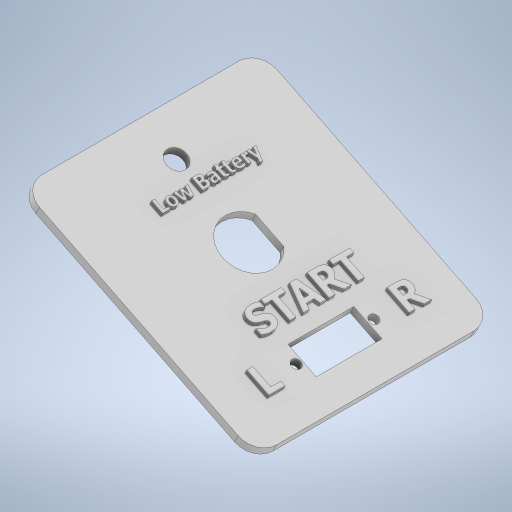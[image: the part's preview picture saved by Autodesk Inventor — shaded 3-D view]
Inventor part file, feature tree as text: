
AUTODESK INVENTOR PART (.ipt)
format: ipt  version: 2024.2 (Build 282272000, 272)  size: 855,552 bytes
history: native  units: mm
features: sketch x10, extrude x9, projected_geometry x4, fillet x2, emboss x1
ambient origin geometry x8: Origin, YZ Plane, XZ Plane, XY Plane, X Axis, Y Axis, Z Axis, Center Point
bodies: Solid1 (feature_tree)
feature tree (26):
  extrude  "Extrusion1"  Depth=2.0mm
  extrude  "Extrusion2"  Depth=6.5mm
  extrude  "Extrusion3"  Depth=9.0mm TaperAngle=0.0deg
  extrude  "Extrusion5"  Depth=9.0mm TaperAngle=0.0deg
  emboss  "Emboss1"
  extrude  "Extrusion6"  Depth=20.0mm
  extrude  "Extrusion7"  Depth=5.0mm
  extrude  "Extrusion8"  Depth=16.3mm
  extrude  "Extrusion9"  Depth=10.0mm
  fillet  "Fillet1"  Radius=20.0mm
  extrude  "Extrusion10"  Depth=8.15mm
  fillet  "Fillet2"  Radius=20.0mm
  sketch  "Sketch2"  dims[d4=2.0mm d5=2.0mm]
  sketch  "Sketch3"  dims[d6=38.25mm d8=6.5mm]
  projected_geometry  "Projected Loop1"
  sketch  "Sketch4"  dims[d9=8.0mm d10=9.0mm d11=0.0mm]
  projected_geometry  "Projected Loop2"
  projected_geometry  "Projected Loop3"
  projected_geometry  "Projected Loop4"
  sketch  "Sketch7"  dims[d12=41.0mm d13=0.0mm d14=9.0mm d15=0.0mm]
  sketch  "Sketch8"  dims[d16=15.0mm d29=20.0mm]
  sketch  "Sketch9"  dims[d30=5.0mm d31=13.0mm]
  sketch  "Sketch10"  dims[d32=29.5mm d33=16.3mm]
  sketch  "Sketch11"  dims[d34=5.2mm d35=10.0mm d36=20.0mm]
  sketch  "Sketch12"  dims[d37=7.8mm d38=8.15mm d39=20.0mm]
  sketch  "Sketch13"  dims[d40=0.0mm d41=0.0mm d42=1.0mm d43=0.0mm d44=49.0mm d45=3.0mm d46=3.0mm d47=3.25mm d48=3.25mm d49=4.0mm d50=2.5mm d51=0.0mm d52=3.0mm d53=3.0mm d54=51.0mm d55=4.0mm d56=4.0mm d57=2.5mm d58=0.0mm d59=135.0deg d60=20.0mm d61=135.0deg d62=20.0mm d63=65.018mm d64=0.0mm d65=0.0mm d66=0.0mm d67=2.3mm d68=2.3mm d69=1.5mm d70=1.5mm d71=3.9mm d72=3.9mm d73=5.0mm d74=4.0mm d75=4.0mm d76=47.0mm d78=48.0mm d79=46.0mm d81=1.0mm d82=12.0mm d83=1.58mm d84=1.5mm d85=0.0mm d86=2.0mm]
